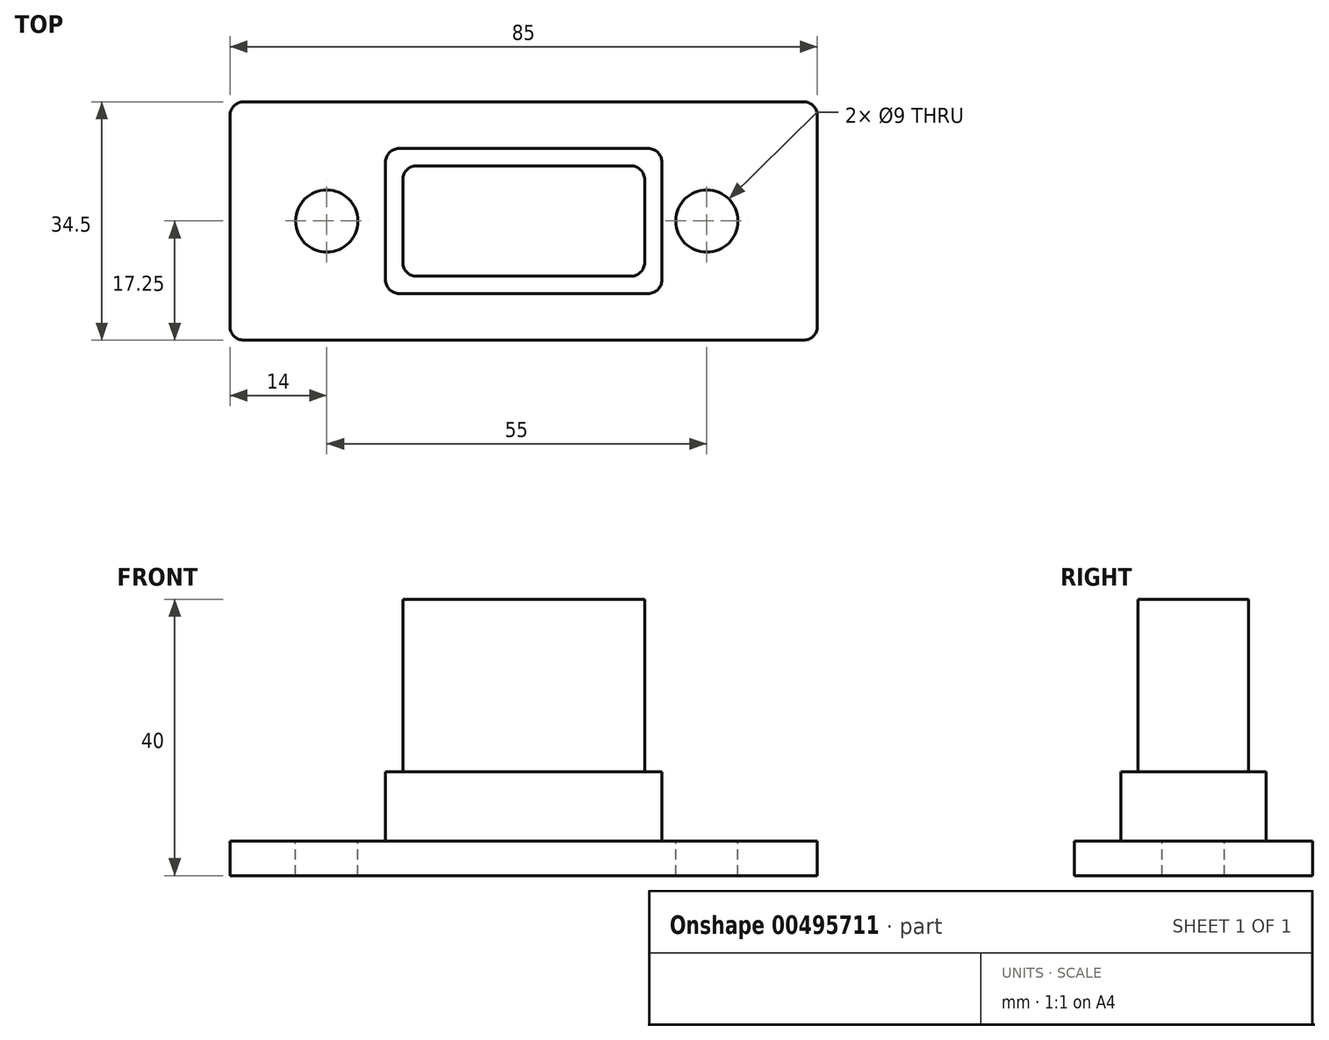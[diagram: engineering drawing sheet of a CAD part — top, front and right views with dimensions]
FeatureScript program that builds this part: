
annotation { "Feature Type Name" : "Feature", "Feature Type Description" : "" }
export const myFeature = defineFeature(function(context is Context, id is Id, definition is map)
    precondition{}
    {
        {
            var Q0;
            Q0=qCreatedBy(makeId("Top.planeOp"),FACE);
            var sketch = newSketch(context, id + "F0", { "sketchPlane" : qUnion([Q0]), "disableImprinting" : false});
            skLineSegment(sketch, "E0.bottom", {"start": v(42.5, 17.25) * mm, "end": v(-42.5, 17.25) * mm});
            skLineSegment(sketch, "E0.top", {"start": v(42.5, -17.25) * mm, "end": v(-42.5, -17.25) * mm});
            skLineSegment(sketch, "E0.left", {"start": v(42.5, 17.25) * mm, "end": v(42.5, -17.25) * mm});
            skLineSegment(sketch, "E0.right", {"start": v(-42.5, 17.25) * mm, "end": v(-42.5, -17.25) * mm});
            skPoint(sketch, "E0.middle", {"position": v(0, 0) * mm});
            skSolve(sketch);
        }
        {
            var Q0;
            Q0=makeQuery(id+"F0.imprint","IMPRINT",FACE,{"disambiguationData":[TD([[makeQuery(id+"F0.imprint","IMPRINT",EDGE,{"derivedFrom":sQuery(id+"F0.wireOp",EDGE,"E0.bottom")}),1.0]])]});
            extrude(context, id + "F1", {"entities" : qUnion([Q0]), "depth" : 5 * mm, "offsetDistance" : 25 * mm});
        }
        {
            var Q0;
            Q0=makeQuery(id+"F1.opExtrude","CAP_FACE",FACE,{"disambiguationData":[OSD([sQuery(id+"F0.wireOp",EDGE,"E0.bottom"),sQuery(id+"F0.wireOp",EDGE,"E0.top"),sQuery(id+"F0.wireOp",EDGE,"E0.left"),sQuery(id+"F0.wireOp",EDGE,"E0.right")])],"isStart":false});
            var sketch = newSketch(context, id + "F2", { "sketchPlane" : qUnion([Q0])});
            skLineSegment(sketch, "E1.bottom", {"start": v(20, -10.5) * mm, "end": v(-20, -10.5) * mm});
            skLineSegment(sketch, "E1.top", {"start": v(20, 10.5) * mm, "end": v(-20, 10.5) * mm});
            skLineSegment(sketch, "E1.left", {"start": v(20, -10.5) * mm, "end": v(20, 10.5) * mm});
            skLineSegment(sketch, "E1.right", {"start": v(-20, -10.5) * mm, "end": v(-20, 10.5) * mm});
            skPoint(sketch, "E1.middle", {"position": v(0, 0) * mm});
            skSolve(sketch);
        }
        {
            var Q0;
            Q0=makeQuery(id+"F2.imprint","IMPRINT",FACE,{"disambiguationData":[TD([[makeQuery(id+"F2.imprint","IMPRINT",EDGE,{"derivedFrom":sQuery(id+"F2.wireOp",EDGE,"E1.bottom")}),-1.0]])]});
            extrude(context, id + "F3", {"entities" : qUnion([Q0]), "operationType" : NewBodyOperationType.ADD, "depth" : 10 * mm, "offsetDistance" : 25 * mm});
        }
        {
            var Q0;
            Q0=makeQuery(id+"F3.opExtrude","CAP_FACE",FACE,{"disambiguationData":[OSD([sQuery(id+"F2.wireOp",EDGE,"E1.bottom"),sQuery(id+"F2.wireOp",EDGE,"E1.top"),sQuery(id+"F2.wireOp",EDGE,"E1.left"),sQuery(id+"F2.wireOp",EDGE,"E1.right")])],"isStart":false});
            var sketch = newSketch(context, id + "F4", { "sketchPlane" : qUnion([Q0])});
            skLineSegment(sketch, "E2.bottom", {"start": v(17.5, -8) * mm, "end": v(-17.5, -8) * mm});
            skLineSegment(sketch, "E2.top", {"start": v(17.5, 8) * mm, "end": v(-17.5, 8) * mm});
            skLineSegment(sketch, "E2.left", {"start": v(17.5, -8) * mm, "end": v(17.5, 8) * mm});
            skLineSegment(sketch, "E2.right", {"start": v(-17.5, -8) * mm, "end": v(-17.5, 8) * mm});
            skPoint(sketch, "E2.middle", {"position": v(0, 0) * mm});
            skSolve(sketch);
        }
        {
            var Q0;
            Q0=makeQuery(id+"F4.imprint","IMPRINT",FACE,{"disambiguationData":[TD([[makeQuery(id+"F4.imprint","IMPRINT",EDGE,{"derivedFrom":sQuery(id+"F4.wireOp",EDGE,"E2.bottom")}),-1.0]])]});
            extrude(context, id + "F5", {"entities" : qUnion([Q0]), "operationType" : NewBodyOperationType.ADD, "depth" : 25 * mm});
        }
        {
            var Q0;
            Q0=makeQuery(id+"F1.opExtrude","CAP_FACE",FACE,{"disambiguationData":[OSD([sQuery(id+"F0.wireOp",EDGE,"E0.bottom"),sQuery(id+"F0.wireOp",EDGE,"E0.top"),sQuery(id+"F0.wireOp",EDGE,"E0.left"),sQuery(id+"F0.wireOp",EDGE,"E0.right")])],"isStart":false});
            var sketch = newSketch(context, id + "F6", { "sketchPlane" : qUnion([Q0]), "disableImprinting" : false});
            skLineSegment(sketch, "E3", {"start": v(-42.5, 0) * mm, "end": v(-26.5, 0) * mm});
            skLineSegment(sketch, "E4", {"start": v(42.5, 0) * mm, "end": v(26.5, 0) * mm});
            skCircle(sketch, "E5", {"center": v(26.5, 0) * mm, "radius": 4.5 * mm});
            skSolve(sketch);
        }
        {
            var Q0;
            Q0=makeQuery(id+"F6.imprint","IMPRINT",FACE,{"disambiguationData":[TD([[makeQuery(id+"F6.imprint","IMPRINT",EDGE,{"derivedFrom":sQuery(id+"F6.wireOp",EDGE,"E5")}),1.0]])]});
            var Q1;
            Q1=sQuery(id+"F6.wireOp",EDGE,"E5");
            extrude(context, id + "F7", {"entities" : qUnion([Q0]), "operationType" : NewBodyOperationType.REMOVE, "surfaceEntities" : qUnion([Q1]), "oppositeDirection" : true, "depth" : 6 * mm});
        }
        {
            var Q0;
            Q0=makeQuery(id+"F1.opExtrude","CAP_FACE",FACE,{"disambiguationData":[OSD([sQuery(id+"F0.wireOp",EDGE,"E0.bottom"),sQuery(id+"F0.wireOp",EDGE,"E0.top"),sQuery(id+"F0.wireOp",EDGE,"E0.left"),sQuery(id+"F0.wireOp",EDGE,"E0.right")])],"isStart":false});
            var sketch = newSketch(context, id + "F8", { "sketchPlane" : qUnion([Q0]), "disableImprinting" : false});
            skLineSegment(sketch, "E6", {"start": v(-42.5, 0) * mm, "end": v(-28.5, 0) * mm});
            skCircle(sketch, "E7", {"center": v(-28.5, 0) * mm, "radius": 4.5 * mm});
            skSolve(sketch);
        }
        {
            var Q0;
            Q0=makeQuery(id+"F8.imprint","IMPRINT",FACE,{"disambiguationData":[TD([[makeQuery(id+"F8.imprint","IMPRINT",EDGE,{"derivedFrom":sQuery(id+"F8.wireOp",EDGE,"E7")}),1.0]])]});
            extrude(context, id + "F9", {"entities" : qUnion([Q0]), "operationType" : NewBodyOperationType.REMOVE, "oppositeDirection" : true, "depth" : 6 * mm});
        }
        {
            var Q0;
            Q0=makeQuery(id+"F3.opExtrude","SWEPT_EDGE",EDGE,{"disambiguationData":[OSD([sQuery(id+"F2.wireOp",EDGE,"E1.top"),sQuery(id+"F2.wireOp",EDGE,"E1.right")])]});
            var Q1;
            Q1=makeQuery(id+"F3.opExtrude","SWEPT_EDGE",EDGE,{"disambiguationData":[OSD([sQuery(id+"F2.wireOp",EDGE,"E1.bottom"),sQuery(id+"F2.wireOp",EDGE,"E1.right")])]});
            var Q2;
            Q2=makeQuery(id+"F3.opExtrude","SWEPT_EDGE",EDGE,{"disambiguationData":[OSD([sQuery(id+"F2.wireOp",EDGE,"E1.bottom"),sQuery(id+"F2.wireOp",EDGE,"E1.left")])]});
            var Q3;
            Q3=makeQuery(id+"F3.opExtrude","SWEPT_EDGE",EDGE,{"disambiguationData":[OSD([sQuery(id+"F2.wireOp",EDGE,"E1.top"),sQuery(id+"F2.wireOp",EDGE,"E1.left")])]});
            fillet(context, id + "F10", {"entities" : qUnion([Q0, Q1, Q2, Q3]), "radius" : 2 * mm, "tangentPropagation" : true, "allowEdgeOverflow" : false});
        }
        {
            var Q0;
            Q0=makeQuery(id+"F5.opExtrude","SWEPT_EDGE",EDGE,{"disambiguationData":[OSD([sQuery(id+"F4.wireOp",EDGE,"E2.bottom"),sQuery(id+"F4.wireOp",EDGE,"E2.left")])]});
            var Q1;
            Q1=makeQuery(id+"F5.opExtrude","SWEPT_EDGE",EDGE,{"disambiguationData":[OSD([sQuery(id+"F4.wireOp",EDGE,"E2.top"),sQuery(id+"F4.wireOp",EDGE,"E2.left")])]});
            var Q2;
            Q2=makeQuery(id+"F5.opExtrude","SWEPT_EDGE",EDGE,{"disambiguationData":[OSD([sQuery(id+"F4.wireOp",EDGE,"E2.bottom"),sQuery(id+"F4.wireOp",EDGE,"E2.right")])]});
            var Q3;
            Q3=makeQuery(id+"F5.opExtrude","SWEPT_EDGE",EDGE,{"disambiguationData":[OSD([sQuery(id+"F4.wireOp",EDGE,"E2.top"),sQuery(id+"F4.wireOp",EDGE,"E2.right")])]});
            fillet(context, id + "F11", {"entities" : qUnion([Q0, Q1, Q2, Q3]), "radius" : 2 * mm, "tangentPropagation" : true, "allowEdgeOverflow" : false});
        }
        {
            var Q0;
            Q0=makeQuery(id+"F1.opExtrude","SWEPT_EDGE",EDGE,{"disambiguationData":[OSD([sQuery(id+"F0.wireOp",EDGE,"E0.top"),sQuery(id+"F0.wireOp",EDGE,"E0.right")])]});
            var Q1;
            Q1=makeQuery(id+"F1.opExtrude","SWEPT_EDGE",EDGE,{"disambiguationData":[OSD([sQuery(id+"F0.wireOp",EDGE,"E0.top"),sQuery(id+"F0.wireOp",EDGE,"E0.left")])]});
            var Q2;
            Q2=makeQuery(id+"F1.opExtrude","SWEPT_EDGE",EDGE,{"disambiguationData":[OSD([sQuery(id+"F0.wireOp",EDGE,"E0.bottom"),sQuery(id+"F0.wireOp",EDGE,"E0.left")])]});
            var Q3;
            Q3=makeQuery(id+"F1.opExtrude","SWEPT_EDGE",EDGE,{"disambiguationData":[OSD([sQuery(id+"F0.wireOp",EDGE,"E0.bottom"),sQuery(id+"F0.wireOp",EDGE,"E0.right")])]});
            fillet(context, id + "F12", {"entities" : qUnion([Q0, Q1, Q2, Q3]), "radius" : 2 * mm, "tangentPropagation" : true, "allowEdgeOverflow" : false});
        }
    });
